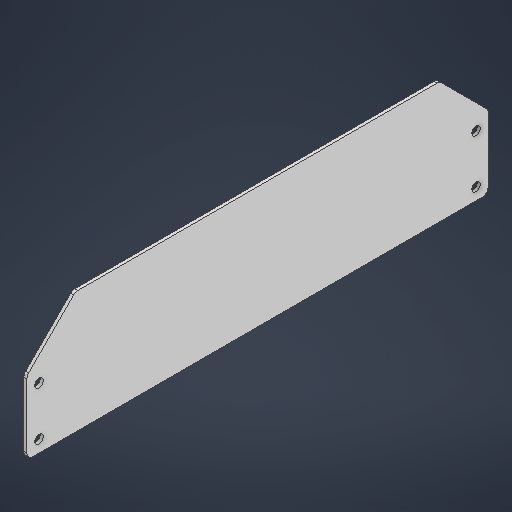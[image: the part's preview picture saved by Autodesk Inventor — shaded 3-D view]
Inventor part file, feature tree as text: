
AUTODESK INVENTOR PART (.ipt)
format: ipt  version: 2025.2 (Build 292293000, 293)  size: 186,880 bytes
history: native  units: in
note: dims shown in document units (in); Inventor stores cm internally (conversion verified against a paired STEP export)
features: extrude x1, sketch x1
ambient origin geometry x8: Origin, YZ Plane, XZ Plane, XY Plane, X Axis, Y Axis, Z Axis, Center Point
bodies: Solid1 (feature_tree)
feature tree (2):
  extrude  "Extrusion1"  Depth=0.0625in TaperAngle=0.0deg
  sketch  "Sketch1"  dims[d0=9.5in d1=1.5in d2=1.5in d3=0.125in d4=0.125in d5=0.125in d6=0.125in d7=0.125in d8=0.125in d9=0.0625in d10=0.0in]
